# Revit family: SPN1260NDWS830O0400xxx
name_source: partatom
category: Leuchten
units: mm (PartAtom-declared; Revit-internal decimal feet)

## family parameters
Basisbauteil = Fläche
Beim Laden mit Abzugskörper schneiden = Nein
Bemaßung runder Anschluss = Durchmesser verwenden
Gemeinsam genutzt = Nein
Lichtquelle = Ja
OmniClass-Nummer = 23.80.70.11
OmniClass-Titel = Luminaries for Internal Lighting
Raumberechnungspunkt = Nein
Teiletyp = Normal

## types (6) — shared parameters
Baugruppenkennzeichen = D5020200
Datei für fotometrisches Netz = SPNxxx O.IES
Emissionsform beim Rendern sichtbar = Nein
Farbfilter = 16777215
Farbtemperaturverschiebung bei Dämpfen der Lampe = <Keine Auswahl>
Hersteller = RIDI Leuchten GmbH
Lampe = LED
Neigungswinkel = 90.00°
Scheinlast = 29 VA
URL = www.ridi.de
Von Breite des Rechtecks ausssenden = 1176 mm  [stored 3.85827 ft]
Von Länge des Rechtecks aussenden = 60 mm  [stored 0.19685 ft]
brand = RIDI
conformity mark = CE
electrical safety class = 1
height = 95 mm
length = 1260 mm  [stored 4.13386 ft]
nominal frequency = 50-60Hz
nominal voltage = 230
rated input power = 29
voltage type (AC, DC, UC) = AC
weight = 2,3 kg
width = 67 mm
zero-valued in all types: Vorgabe-Ansicht

## per-type parameters (varying)
| type | Modell | ingress protection (IP) code |
| SPN1260NDWS830O0400 | 0422202 | IP40 |
| SPN1260NDWS840O0400 | 0422205 | IP40 |
| SPN1260NDWS830O0400-S | 0422203 | IP40 |
| SPN1260NDWS840O0400-S | 0422206 | IP40 |
| SPN1260NDWS830O0400-ST | 0422204 | IP20 |
| SPN1260NDWS840O0400-ST | 0422207 | IP20 |

note: column(s) folded — value = type name in every type: product name

note: [stored X ft] marks values corroborated as IEEE doubles in the binary element streams (Revit-internal decimal feet)
